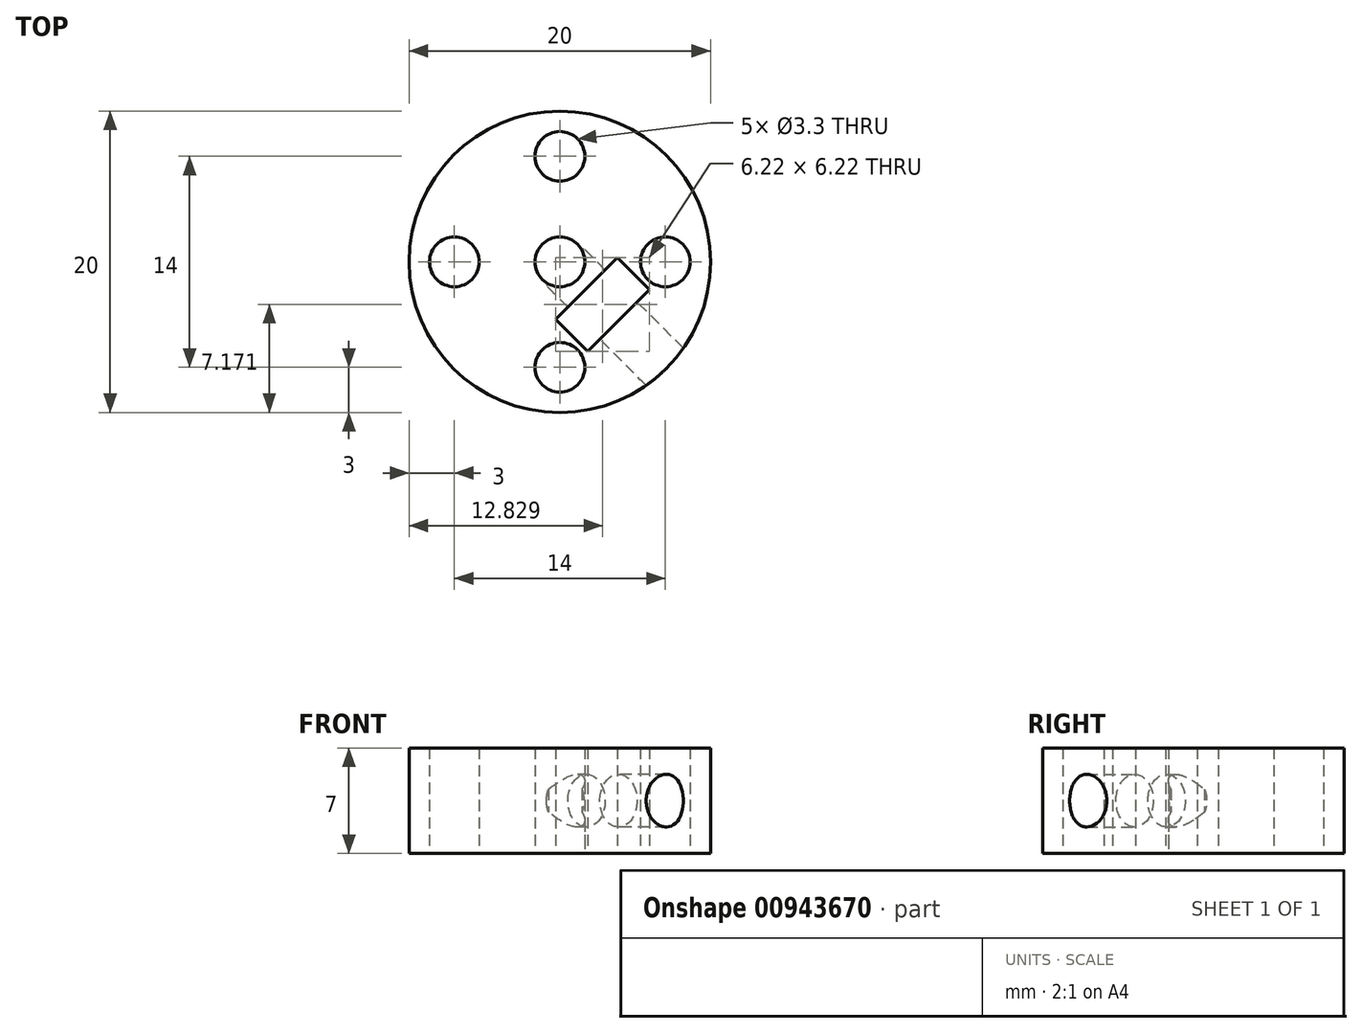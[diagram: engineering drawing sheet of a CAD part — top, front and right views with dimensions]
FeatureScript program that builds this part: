
annotation { "Feature Type Name" : "Feature", "Feature Type Description" : "" }
export const myFeature = defineFeature(function(context is Context, id is Id, definition is map)
    precondition{}
    {
        {
            var Q0;
            Q0=qCreatedBy(makeId("Top.planeOp"),FACE);
            var sketch = newSketch(context, id + "F0", { "sketchPlane" : qUnion([Q0])});
            skCircle(sketch, "E0", {"center": v(0, 0) * mm, "radius": 10 * mm});
            skCircle(sketch, "E1", {"center": v(0, 7) * mm, "radius": 1.65 * mm});
            skCircle(sketch, "E2.1.0", {"center": v(-7, 0) * mm, "radius": 1.65 * mm});
            skCircle(sketch, "E2.2.0", {"center": v(0, -7) * mm, "radius": 1.65 * mm});
            skCircle(sketch, "E2.3.0", {"center": v(7, 0) * mm, "radius": 1.65 * mm});
            skCircle(sketch, "E3", {"center": v(0, 0) * mm, "radius": 1.65 * mm});
            skLineSegment(sketch, "E4", {"start": v(0, 0) * mm, "end": v(2.83, -2.83) * mm});
            skLineSegment(sketch, "E5.bottom", {"start": v(-0.28, -3.82) * mm, "end": v(1.84, -5.94) * mm});
            skLineSegment(sketch, "E5.top", {"start": v(3.82, 0.28) * mm, "end": v(5.94, -1.84) * mm});
            skLineSegment(sketch, "E5.left", {"start": v(-0.28, -3.82) * mm, "end": v(3.82, 0.28) * mm});
            skLineSegment(sketch, "E5.right", {"start": v(1.84, -5.94) * mm, "end": v(5.94, -1.84) * mm});
            skPoint(sketch, "E5.middle", {"position": v(2.83, -2.83) * mm});
            skSolve(sketch);
        }
        {
            var Q0;
            Q0=makeQuery(id+"F0.imprint","IMPRINT",FACE,{"disambiguationData":[TD([[makeQuery(id+"F0.imprint","IMPRINT",EDGE,{"derivedFrom":sQuery(id+"F0.wireOp",EDGE,"E0")}),1.0]])]});
            extrude(context, id + "F1", {"entities" : qUnion([Q0]), "depth" : 7 * mm, "offsetDistance" : 25 * mm});
        }
        {
            var Q0;
            Q0=makeQuery(id+"F1.opExtrude","SWEPT_FACE",FACE,{"disambiguationData":[OSD([sQuery(id+"F0.wireOp",EDGE,"E5.right")])]});
            var sketch = newSketch(context, id + "F2", { "sketchPlane" : qUnion([Q0])});
            skCircle(sketch, "E6", {"center": v(0, 3.5) * mm, "radius": 1.75 * mm});
            skPoint(sketch, "E6.centerSnap0", {"position": v(-2.9, 3.5) * mm});
            skPoint(sketch, "E6.centerSnap1", {"position": v(0, 7) * mm});
            skSolve(sketch);
        }
        {
            var Q0;
            Q0 = qSketchRegion(id + "F2", true);
            extrude(context, id + "F3", {"entities" : qUnion([Q0]), "operationType" : NewBodyOperationType.REMOVE, "oppositeDirection" : true, "depth" : 25 * mm, "offsetDistance" : 25 * mm, "hasSecondDirection" : true, "secondDirectionOppositeDirection" : false, "secondDirectionDepth" : 5 * mm});
        }
    });
